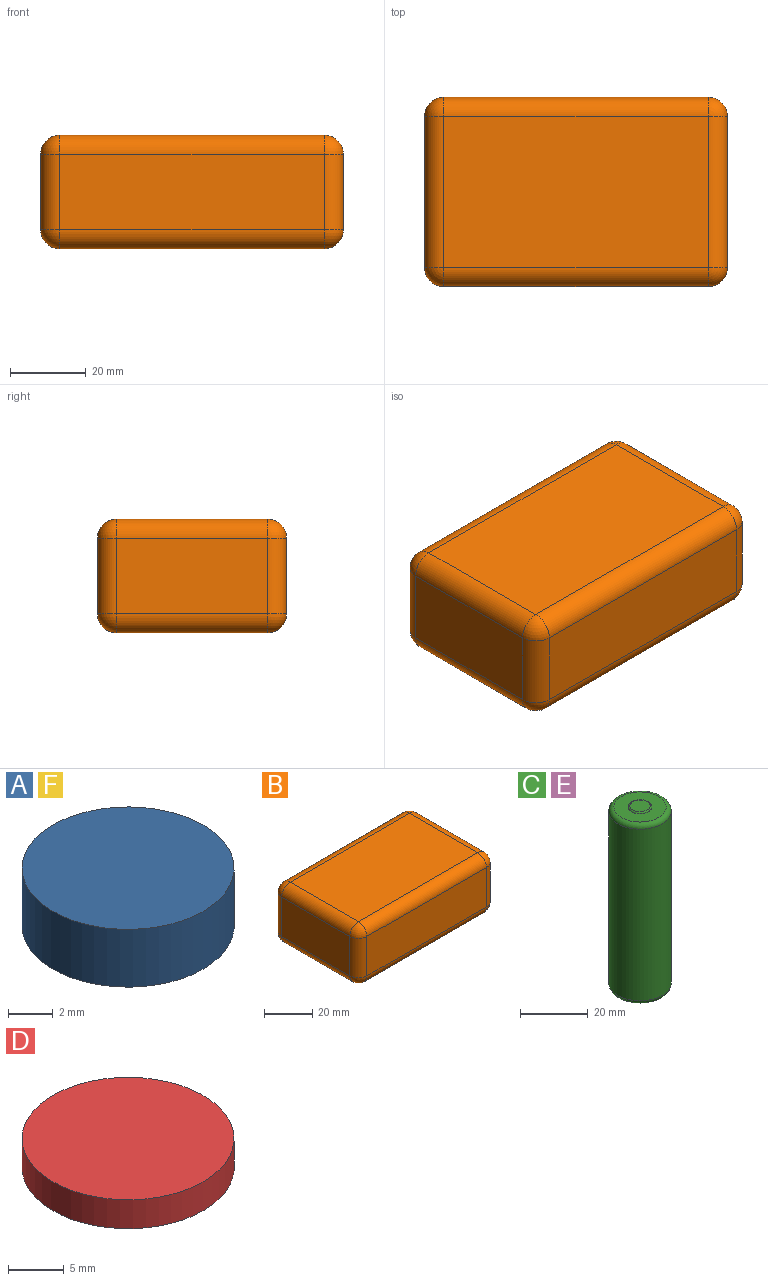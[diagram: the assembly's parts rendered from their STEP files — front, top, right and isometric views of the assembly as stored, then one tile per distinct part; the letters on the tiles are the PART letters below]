
ASSEMBLY  parts=6 mates=4
PART A: 3 faces, bbox 9.5x9.5x3.2 mm
  f0: cylinder r=4.76mm len=9.53mm, axis (0,0,-1), area 95mm2, adj f1,f2
  f1: plane 9.53x9.53mm, normal (0,0,1), area 71.3mm2, adj f0
  f2: plane 9.53x9.53mm, normal (0,0,-1), area 71.3mm2, adj f0
PART B: 39 faces, bbox 80x50x30 mm
  f0: plane 70x40mm, normal (0,0,1), area 2800mm2, adj f13,f14,f23,f24
  f1: plane 40x20mm, normal (-1,0,0), area 800mm2, adj f10,f14,f15,f16
  f2: plane 70x40mm, normal (0,0,-1), area 2445mm2, adj f16,f17,f25,f26,f36,f37,f38
  f3: plane 70x20mm, normal (0,-1,0), area 1400mm2, adj f10,f13,f17,f18
  f4: plane 70x20mm, normal (0,1,0), area 1400mm2, adj f15,f24,f25,f29
  f5: plane 75x20mm, normal (0,1,0), area 1500mm2, adj f6,f7,f8,f18
  f6: plane 75x40mm, normal (0,0,-1), area 3000mm2, adj f5,f8,f9,f23
  f7: plane 75x40mm, normal (0,0,1), area 2528.8mm2, adj f5,f8,f9,f26,f30,f32,f34
  f8: plane 40x20mm, normal (1,0,0), area 800mm2, adj f5,f6,f7,f9
  f9: plane 75x20mm, normal (0,-1,0), area 1500mm2, adj f6,f7,f8,f29
  f10: cylinder r=5mm len=20mm, axis (0,0,1), area 157.1mm2, adj f1,f3,f11,f12
  f11: sphere r=5mm, area 39.3mm2, adj f10,f13,f14
  f12: sphere r=5mm, area 39.3mm2, adj f10,f16,f17
  f13: cylinder r=5mm len=70mm, axis (1,0,0), area 549.8mm2, adj f0,f3,f11,f19
  f14: cylinder r=5mm len=40mm, axis (0,-1,0), area 314.2mm2, adj f0,f1,f11,f20
  f15: cylinder r=5mm len=20mm, axis (0,0,1), area 157.1mm2, adj f1,f4,f20,f21
  f16: cylinder r=5mm len=40mm, axis (0,1,0), area 314.2mm2, adj f1,f2,f12,f21
  f17: cylinder r=5mm len=70mm, axis (-1,0,0), area 549.8mm2, adj f2,f3,f12,f22
  f18: cylinder r=5mm len=20mm, axis (0,0,-1), area 157.1mm2, adj f3,f5,f19,f22
  f19: sphere r=5mm, area 39.3mm2, adj f13,f18,f23
  f20: sphere r=5mm, area 39.3mm2, adj f14,f15,f24
  f21: sphere r=5mm, area 39.3mm2, adj f15,f16,f25
  f22: sphere r=5mm, area 39.3mm2, adj f17,f18,f26
  f23: cylinder r=5mm len=40mm, axis (0,1,0), area 314.2mm2, adj f0,f6,f19,f27
  f24: cylinder r=5mm len=70mm, axis (1,0,0), area 549.8mm2, adj f0,f4,f20,f27
  f25: cylinder r=5mm len=70mm, axis (-1,0,0), area 549.8mm2, adj f2,f4,f21,f28
  f26: cylinder r=5mm len=40mm, axis (0,-1,0), area 314.2mm2, adj f2,f7,f22,f28
  f27: sphere r=5mm, area 39.3mm2, adj f23,f24,f29
  f28: sphere r=5mm, area 39.3mm2, adj f25,f26,f29
  f29: cylinder r=5mm len=20mm, axis (0,0,-1), area 157.1mm2, adj f4,f9,f27,f28
  f30: cylinder r=5mm len=10mm, axis (0,0,1), area 94.2mm2, adj f7,f31
  f31: plane 10x10mm, normal (0,0,1), area 28.3mm2, adj f30,f36
  f32: cylinder r=5mm len=10mm, axis (0,0,1), area 94.2mm2, adj f7,f33
  f33: plane 10x10mm, normal (0,0,1), area 28.3mm2, adj f32,f37
  f34: cylinder r=10mm len=20mm, axis (0,0,1), area 188.5mm2, adj f7,f35
  f35: plane 20x20mm, normal (0,0,1), area 59.7mm2, adj f34,f38
  f36: cylinder r=4mm len=8mm, axis (0,0,-1), area 50.3mm2, adj f2,f31
  f37: cylinder r=4mm len=8mm, axis (0,0,-1), area 50.3mm2, adj f2,f33
  f38: cylinder r=9mm len=18mm, axis (0,0,-1), area 113.1mm2, adj f2,f35
PART C: 10 faces, bbox 20x20x66.9 mm
  f0: cylinder r=9.25mm len=62.25mm, axis (0,0,-1), area 3618.1mm2, adj f3,f4
  f1: plane 15.45x15.45mm, normal (0,0,1), area 148.9mm2, adj f3,f6
  f2: plane 15.45x15.45mm, normal (0,0,-1), area 167.9mm2, adj f4,f7
  f3: torus R=7.73mm, axis (0,0,1), area 130.8mm2, adj f0,f1
  f4: torus R=7.73mm, axis (0,0,1), area 130.8mm2, adj f0,f2
  f5: plane 6.02x6.02mm, normal (0,0,1), area 28.4mm2, adj f6
  f6: torus R=3.01mm, axis (0,0,-1), area 14.4mm2, adj f1,f5
  f7: cylinder r=2.5mm len=5mm, axis (0,0,1), area 6.8mm2, adj f2,f9
  f8: plane 3.48x3.48mm, normal (0,0,-1), area 9.5mm2, adj f9
  f9: torus R=1.74mm, axis (0,0,-1), area 16.7mm2, adj f7,f8
PART D: 3 faces, bbox 19.1x19.1x3.2 mm
  f0: cylinder r=9.53mm len=19.05mm, axis (0,0,-1), area 190mm2, adj f1,f2
  f1: plane 19.05x19.05mm, normal (0,0,1), area 285mm2, adj f0
  f2: plane 19.05x19.05mm, normal (0,0,-1), area 285mm2, adj f0
PART E: same geometry as C
PART F: same geometry as A
PLACE A t=(28.67,-11.25,-9.19)mm
PLACE B t=(8.67,18.75,2.22)mm fixed
PLACE C rot(axis=(0.71,0,-0.71),180deg) t=(11.1,-11.3,3.03)mm
PLACE D t=(-11.33,-1.25,-9.19)mm
PLACE E rot(axis=(0,1,0),90deg) t=(8.2,8.3,2.14)mm
PLACE F t=(28.67,8.75,-9.19)mm
MATE fastened D.f0 <-> B.f34  axis (0,0,-1) through (-11.33,-1.25,-10.78)mm
MATE fastened F.f0 <-> B.f30  axis (0,0,-1) through (28.67,8.75,-10.78)mm
MATE fastened A.f0 <-> B.f32  axis (0,0,-1) through (28.67,-11.25,-10.78)mm
MATE parallel C.f0 <-> B.f8  axis (-1,0,0) through (-21.95,-11.3,3.03)mm
